# Revit family: Дверь ДПО-130
name_source: partatom
category: Двери
revit_build: Autodesk Revit 2017 (Build: 20160225_1515(x64)
units: mm (PartAtom-declared; Revit-internal decimal feet)

## family parameters
Всегда вертикально = Да
Заголовок OmniClass = Doors
Номер OmniClass = 23.30.10.00
Общий = Нет
Основа = Стена
При загрузке вырезать с полостями = Нет
Точка расчета площади = Нет

## types (10) — shared parameters
Выступ каркаса внут. = 25 мм
Выступ каркаса нар. = 25 мм
Группа модели = ДПО-Огнедекор
Замыкание стены = По основе
Изготовитель = ДВР Центр, г.Москва
Огнестойкость = EIW-30
Описание = Дверь противопожарная остекленная
Толщина = 50 мм
Функция = Внутренние слои
Ширина каркаса = 75 мм

## per-type parameters (varying)
| type | Высота | Левая | Материал_коробки | Материал_створки | Правая | Ширина | Ширина створки |
| ДПО-Огнедекор-01/30 21-9 ПТ | 2070 мм | Нет | Сталь, голубой | Сталь, голубой | Да | 870 мм | 770 мм |
| ДПО-Огнедекор-01/30 21-8 ПТ | 2070 мм | Нет | Сталь, голубой | Сталь, голубой | Да | 770 мм | 670 мм |
| ДПО-Огнедекор-01/30 21-7 ПТ | 2070 мм | Нет | Сталь, голубой | Сталь, голубой | Да | 670 мм | 570 мм |
| ДПО-Огнедекор-01/30 21-10 ПТ | 2070 мм | Нет | Сталь, голубой | Сталь, голубой | Да | 970 мм | 870 мм |
| ДПО-Огнедекор-01/30 24-10 ПТ | 2370 мм | Нет | Сталь, белый | Сталь, белый | Да | 970 мм | 870 мм |
| ДПО-Огнедекор-01/30 24-10 ЛТ | 2370 мм | Да | Сталь, голубой | Сталь, голубой | Нет | 970 мм | 870 мм |
| ДПО-Огнедекор-01/30 21-9 ЛТ | 2070 мм | Да | Сталь, голубой | Сталь, голубой | Нет | 870 мм | 770 мм |
| ДПО-Огнедекор-01/30 21-8 ЛТ | 2070 мм | Да | Сталь, голубой | Сталь, голубой | Нет | 770 мм | 670 мм |
| ДПО-Огнедекор-01/30 21-7 ЛТ | 2070 мм | Да | Сталь, голубой | Сталь, голубой | Нет | 670 мм | 570 мм |
| ДПО-Огнедекор-01/30 21-10 ЛТ | 2070 мм | Да | Сталь, голубой | Сталь, голубой | Нет | 970 мм | 870 мм |
